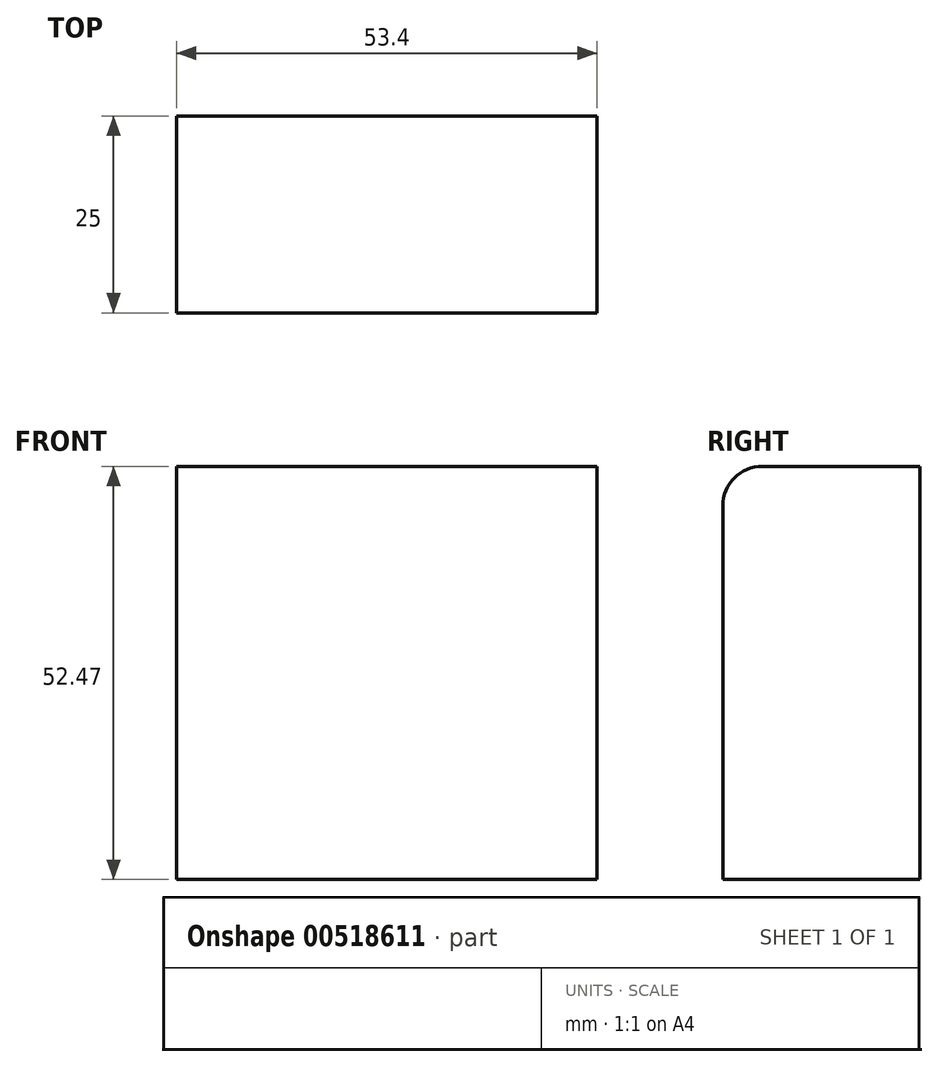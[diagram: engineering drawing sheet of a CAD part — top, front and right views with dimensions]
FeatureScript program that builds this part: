
annotation { "Feature Type Name" : "Feature", "Feature Type Description" : "" }
export const myFeature = defineFeature(function(context is Context, id is Id, definition is map)
    precondition{}
    {
        {
            var Q0;
            Q0=qCreatedBy(makeId("Front.planeOp"),FACE);
            var sketch = newSketch(context, id + "F0", { "sketchPlane" : qUnion([Q0])});
            skLineSegment(sketch, "E0.bottom", {"start": v(-104.64, 0) * mm, "end": v(-51.24, 0) * mm});
            skLineSegment(sketch, "E0.top", {"start": v(-104.64, 52.47) * mm, "end": v(-51.24, 52.47) * mm});
            skLineSegment(sketch, "E0.left", {"start": v(-104.64, 0) * mm, "end": v(-104.64, 52.47) * mm});
            skLineSegment(sketch, "E0.right", {"start": v(-51.24, 0) * mm, "end": v(-51.24, 52.47) * mm});
            skPoint(sketch, "E0.middle", {"position": v(-77.94, 26.23) * mm});
            skSolve(sketch);
        }
        {
            var Q0;
            Q0=makeQuery(id+"F0.imprint","IMPRINT",FACE,{"disambiguationData":[TD([[makeQuery(id+"F0.imprint","IMPRINT",EDGE,{"derivedFrom":sQuery(id+"F0.wireOp",EDGE,"E0.bottom")}),1.0]])]});
            extrude(context, id + "F1", {"entities" : qUnion([Q0]), "depth" : 25 * mm, "offsetDistance" : 25 * mm});
        }
        {
            var Q0;
            Q0=makeQuery(id+"F1.opExtrude","CAP_EDGE",EDGE,{"disambiguationData":[OSD([sQuery(id+"F0.wireOp",EDGE,"E0.top")])],"isStart":false});
            fillet(context, id + "F2", {"entities" : qUnion([Q0]), "radius" : 5 * mm, "tangentPropagation" : true, "allowEdgeOverflow" : false});
        }
    });
